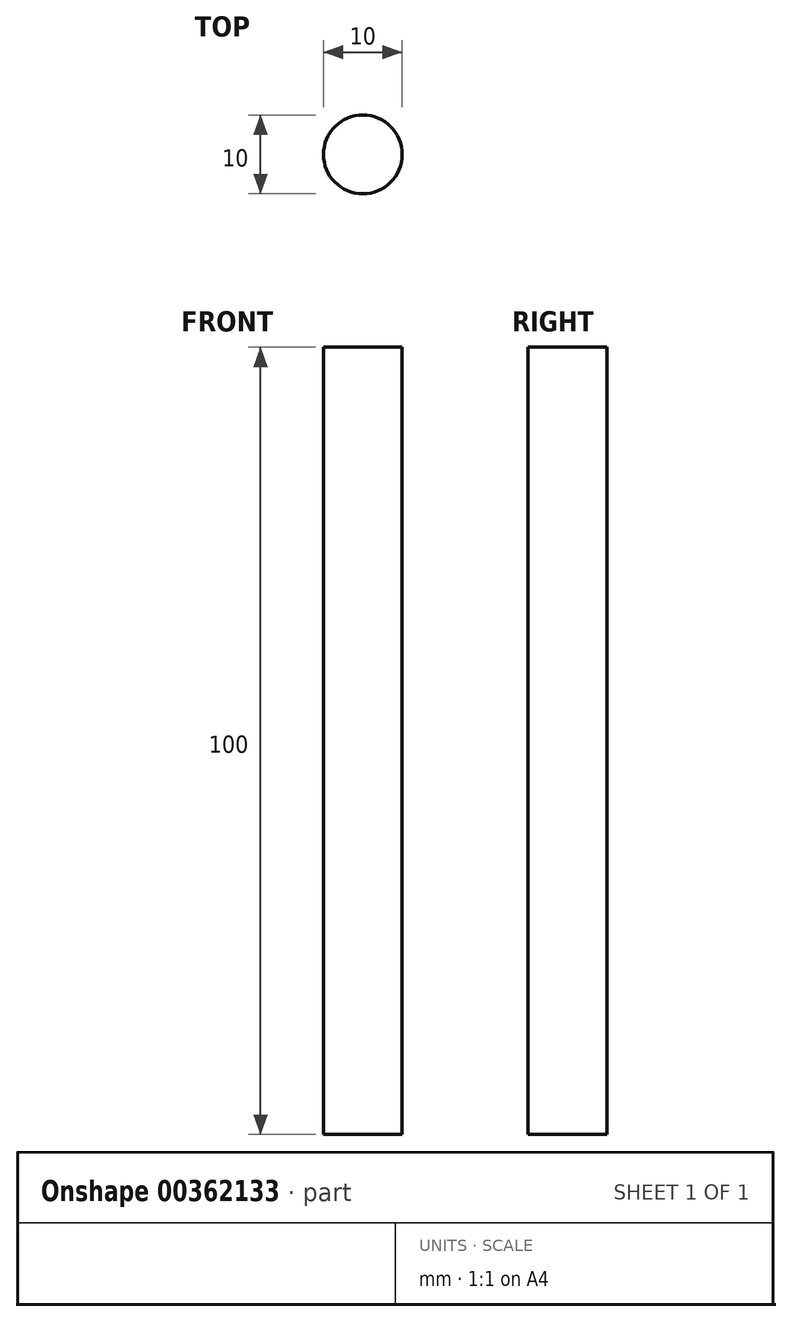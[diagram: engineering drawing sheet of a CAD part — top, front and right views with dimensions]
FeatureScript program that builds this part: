
annotation { "Feature Type Name" : "Feature", "Feature Type Description" : "" }
export const myFeature = defineFeature(function(context is Context, id is Id, definition is map)
    precondition{}
    {
        {
            var Q0;
            Q0=qCreatedBy(makeId("Top.planeOp"),FACE);
            var sketch = newSketch(context, id + "F0", { "sketchPlane" : qUnion([Q0])});
            skCircle(sketch, "E0", {"center": v(0, 0) * mm, "radius": 5 * mm});
            skSolve(sketch);
        }
        {
            var Q0;
            Q0=makeQuery(id+"F0.imprint","IMPRINT",FACE,{"disambiguationData":[TD([[makeQuery(id+"F0.imprint","IMPRINT",EDGE,{"derivedFrom":sQuery(id+"F0.wireOp",EDGE,"E0")}),1.0]])]});
            extrude(context, id + "F1", {"entities" : qUnion([Q0]), "depth" : 100 * mm, "offsetDistance" : 25 * mm});
        }
    });
